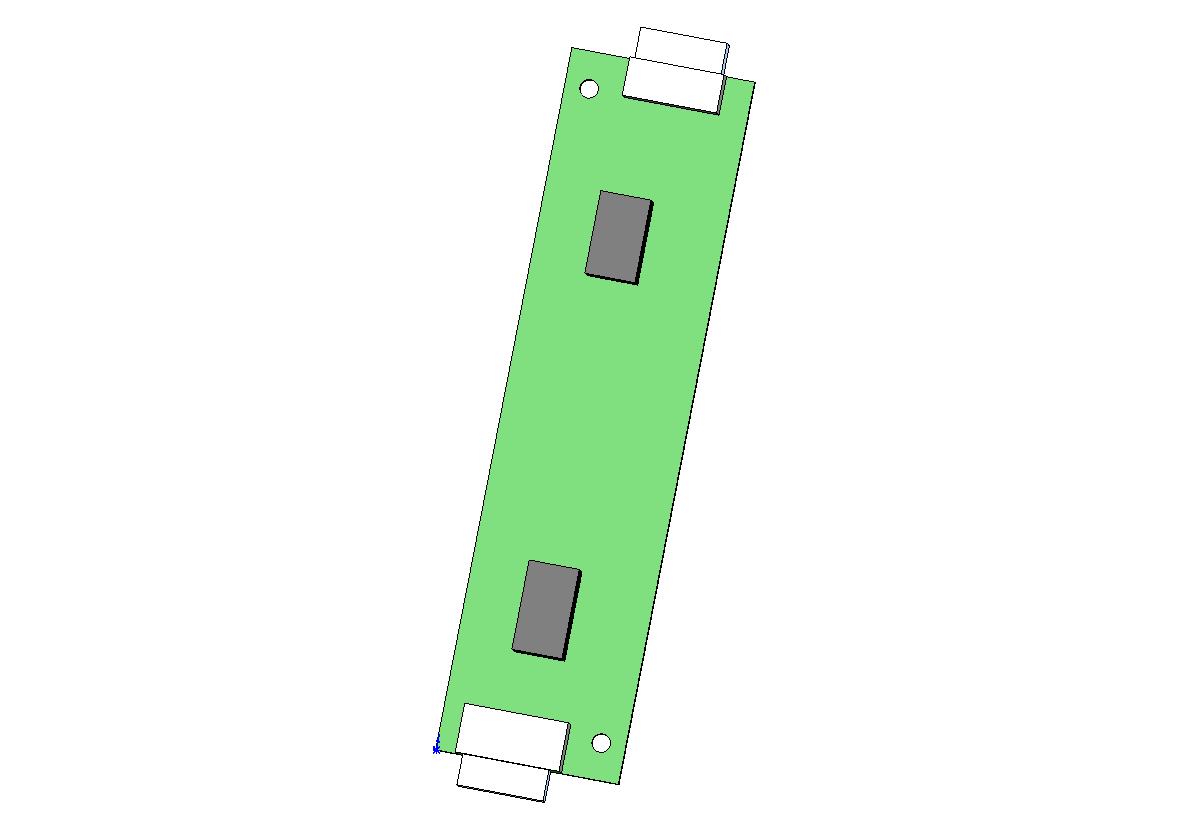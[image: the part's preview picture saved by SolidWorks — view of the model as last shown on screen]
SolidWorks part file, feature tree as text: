
SOLIDWORKS PART (.sldprt)
format: sldprt  version: not decoded by parser v0  size: 152,576 bytes
history: native  units: mm
features: sketch x6, extrude x5, material x1, cut_extrude x1 (+13 scaffold rows collapsed)
feature tree (26):
  scaffold x13  (default folders/planes/origin — collapsed)
  material  "Material <not specified>"
  sketch  "Sketch1"  dims[D1=115.0mm D2=30.0mm]
  extrude  "Extrude1"  Depth=1mm
  sketch  "Sketch2"  dims[D1=3.0mm D2=3.0mm D3=4.0mm D4=6.0mm D5=26.0mm D6=109.0mm]
  cut_extrude  "mount holes - cut"  Depth=1mm
  sketch  "Sketch4"
  extrude  "inductors"  Depth=5.5mm
  sketch  "Sketch5"
  extrude  "ccfl conn"  Depth=5mm
  sketch  "Sketch6"
  extrude  "mate and wire stick-out 1"  Depth=5.08mm
  sketch  "Sketch7"
  extrude  "mate and wire stick-out 2"  Depth=5.08mm
decode coverage: 8 of 12 modeling features carry decoded parameters
note: suppression state not decoded; provenance and decode notes live in map.json
